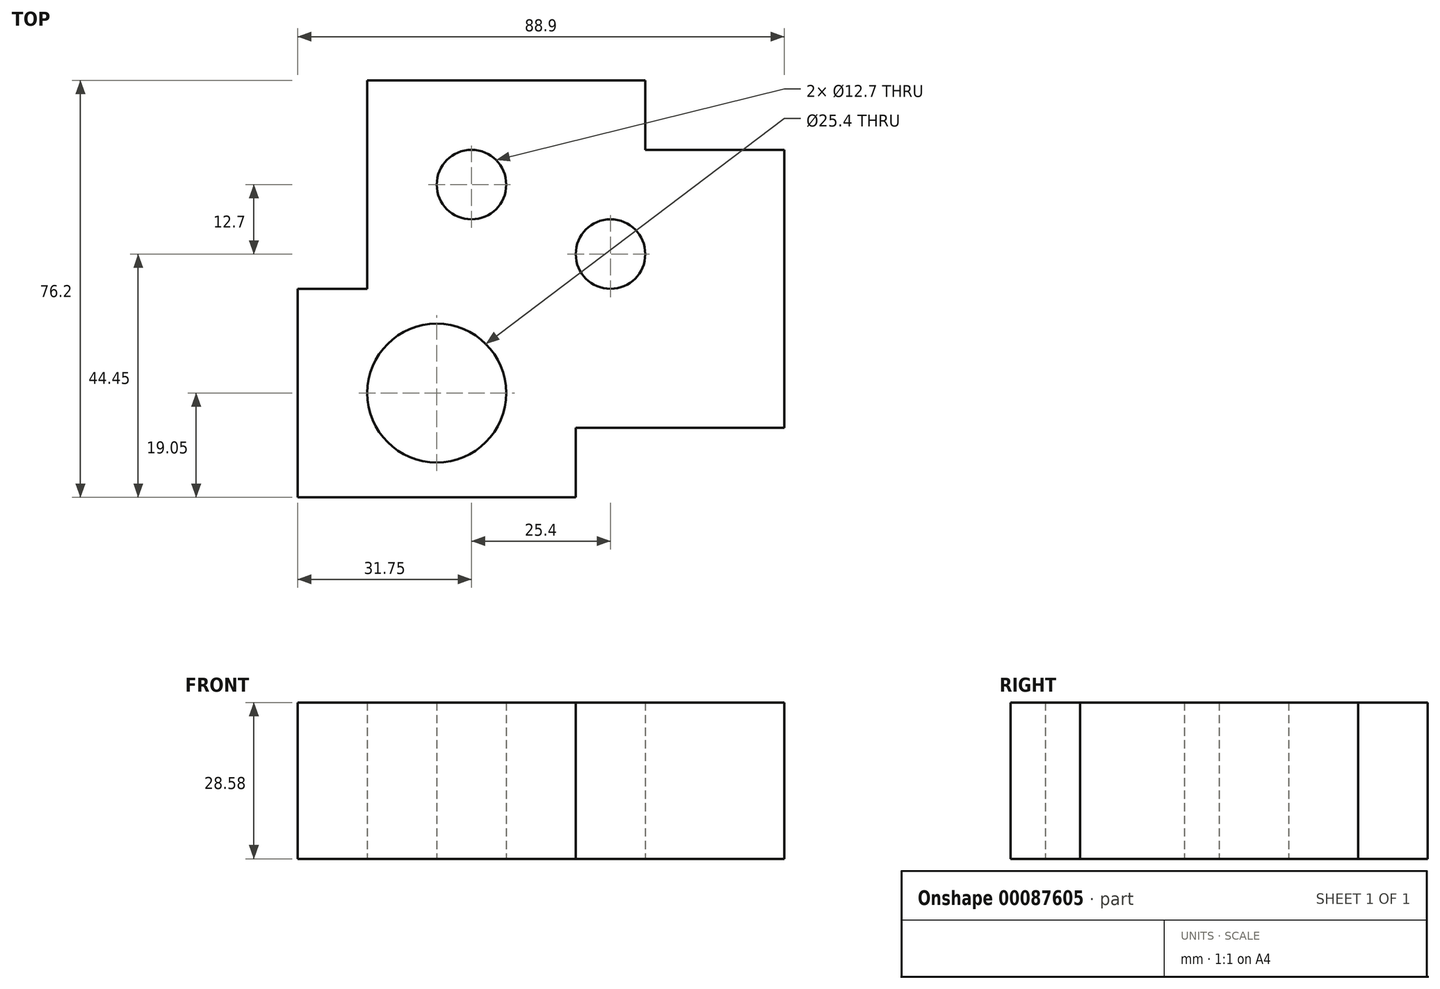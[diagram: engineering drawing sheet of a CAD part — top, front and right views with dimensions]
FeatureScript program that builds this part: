
annotation { "Feature Type Name" : "Feature", "Feature Type Description" : "" }
export const myFeature = defineFeature(function(context is Context, id is Id, definition is map)
    precondition{}
    {
        {
            var Q0;
            Q0=qCreatedBy(makeId("Top.planeOp"),FACE);
            var sketch = newSketch(context, id + "F0", { "sketchPlane" : qUnion([Q0])});
            skLineSegment(sketch, "E0.bottom", {"start": v(0, 0) * mm, "end": v(50.8, 0) * mm});
            skLineSegment(sketch, "E0.top", {"start": v(12.7, 76.2) * mm, "end": v(63.5, 76.2) * mm});
            skLineSegment(sketch, "E0.left", {"start": v(0, 0) * mm, "end": v(0, 38.1) * mm});
            skLineSegment(sketch, "E0.right", {"start": v(88.9, 12.7) * mm, "end": v(88.9, 63.5) * mm});
            skLineSegment(sketch, "E1.top", {"start": v(0, 38.1) * mm, "end": v(12.7, 38.1) * mm});
            skLineSegment(sketch, "E1.right", {"start": v(12.7, 76.2) * mm, "end": v(12.7, 38.1) * mm});
            skLineSegment(sketch, "E2.top", {"start": v(88.9, 63.5) * mm, "end": v(63.5, 63.5) * mm});
            skLineSegment(sketch, "E2.right", {"start": v(63.5, 76.2) * mm, "end": v(63.5, 63.5) * mm});
            skLineSegment(sketch, "E3.top", {"start": v(88.9, 12.7) * mm, "end": v(50.8, 12.7) * mm});
            skLineSegment(sketch, "E3.right", {"start": v(50.8, 0) * mm, "end": v(50.8, 12.7) * mm});
            skCircle(sketch, "E4", {"center": v(25.4, 19.05) * mm, "radius": 12.7 * mm});
            skCircle(sketch, "E5", {"center": v(31.75, 57.15) * mm, "radius": 6.35 * mm});
            skCircle(sketch, "E6", {"center": v(57.15, 44.45) * mm, "radius": 6.35 * mm});
            skSolve(sketch);
        }
        {
            var Q0;
            Q0 = qSketchRegion(id + "F0", true);
            extrude(context, id + "F1", {"entities" : qUnion([Q0]), "depth" : 28.57 * mm});
        }
    });
